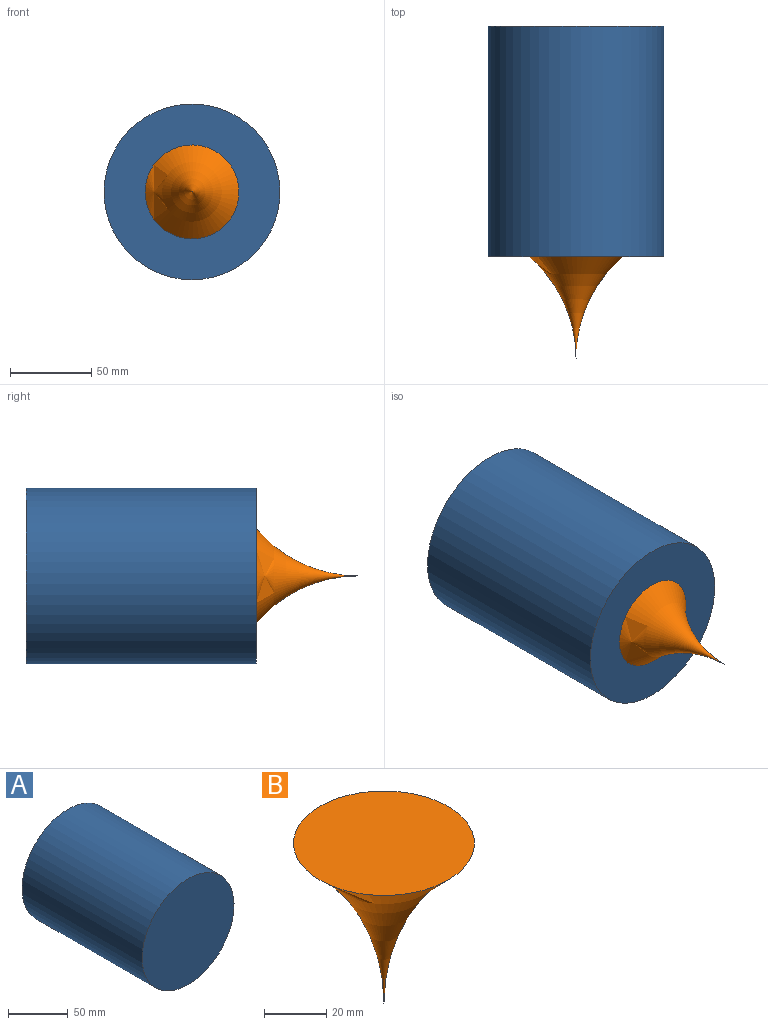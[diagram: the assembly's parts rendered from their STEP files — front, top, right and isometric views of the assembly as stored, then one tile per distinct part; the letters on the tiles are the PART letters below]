
ASSEMBLY  parts=2 mates=1
PART A: 3 faces, bbox 108.5x142x108.5 mm
  f0: cylinder r=54.23mm len=142mm, axis (0,1,0), area 48381.7mm2, adj f1,f2
  f1: plane 108.45x108.45mm, normal (0,-1,0), area 9238mm2, adj f0
  f2: plane 108.45x108.45mm, normal (0,1,0), area 9238mm2, adj f0
PART B: 2 faces, bbox 178x178x82.2 mm
  f0: torus R=82.24mm, axis (0,0,-1), area 4435.9mm2, adj f1
  f1: plane 57.96x57.96mm, normal (0,0,1), area 2638.7mm2, adj f0
PLACE A t=(-59.12,56.2,28.99)mm fixed
PLACE B rot(axis=(-1,0,0),90deg) t=(-59.12,-148.47,28.99)mm
MATE fastened B.f0 <-> A.f0  axis (0,1,0) through (-59.12,-85.8,28.99)mm
